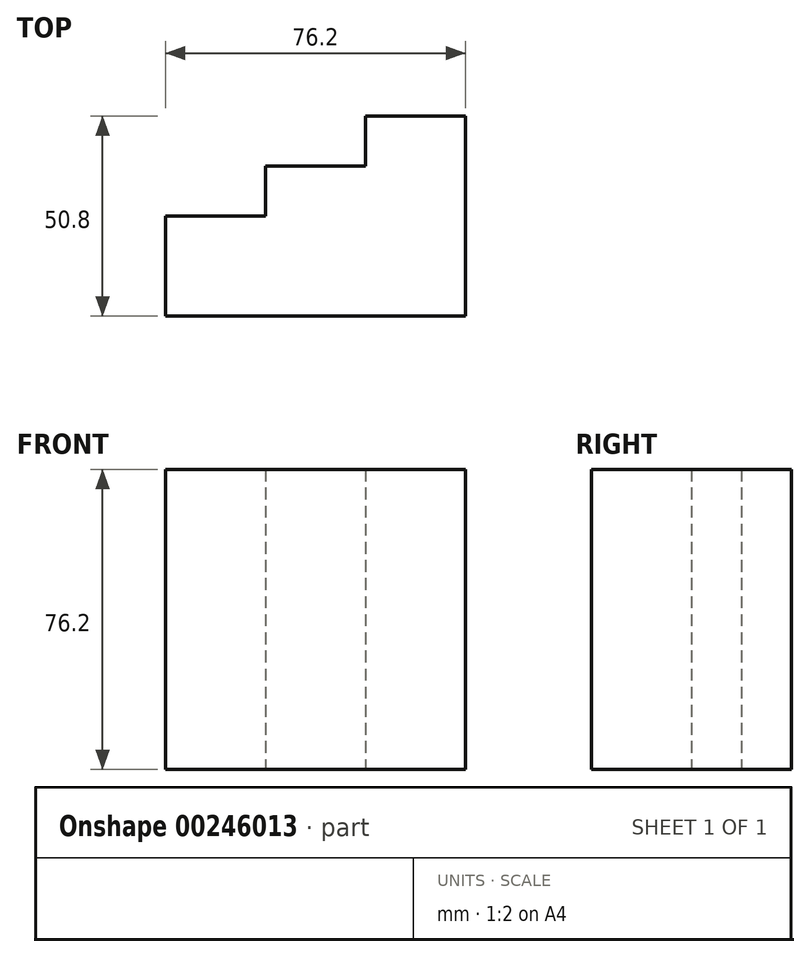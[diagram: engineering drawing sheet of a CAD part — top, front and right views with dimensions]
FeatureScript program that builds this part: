
annotation { "Feature Type Name" : "Feature", "Feature Type Description" : "" }
export const myFeature = defineFeature(function(context is Context, id is Id, definition is map)
    precondition{}
    {
        {
            var Q0;
            Q0=qCreatedBy(makeId("Top.planeOp"),FACE);
            var sketch = newSketch(context, id + "F0", { "sketchPlane" : qUnion([Q0])});
            skLineSegment(sketch, "E0", {"start": v(0, 0) * mm, "end": v(0, 25.4) * mm});
            skLineSegment(sketch, "E1", {"start": v(0, 25.4) * mm, "end": v(25.4, 25.4) * mm});
            skLineSegment(sketch, "E2", {"start": v(25.4, 25.4) * mm, "end": v(25.4, 38.1) * mm});
            skLineSegment(sketch, "E3", {"start": v(25.4, 38.1) * mm, "end": v(50.8, 38.1) * mm});
            skLineSegment(sketch, "E4", {"start": v(50.8, 38.1) * mm, "end": v(50.8, 50.8) * mm});
            skLineSegment(sketch, "E5", {"start": v(50.8, 50.8) * mm, "end": v(76.2, 50.8) * mm});
            skLineSegment(sketch, "E6", {"start": v(76.2, 50.8) * mm, "end": v(76.2, 0) * mm});
            skLineSegment(sketch, "E7", {"start": v(76.2, 0) * mm, "end": v(0, 0) * mm});
            skSolve(sketch);
        }
        {
            var Q0;
            Q0=makeQuery(id+"F0.imprint","IMPRINT",FACE,{"disambiguationData":[TD([[makeQuery(id+"F0.imprint","IMPRINT",EDGE,{"derivedFrom":sQuery(id+"F0.wireOp",EDGE,"E0")}),-1.0]])]});
            extrude(context, id + "F1", {"entities" : qUnion([Q0]), "depth" : 76.2 * mm});
        }
    });
